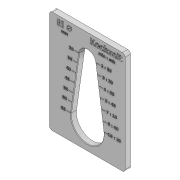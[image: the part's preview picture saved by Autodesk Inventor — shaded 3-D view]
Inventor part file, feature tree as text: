
AUTODESK INVENTOR PART (.ipt)
format: ipt  version: 2020 (Build 240168000, 168)  size: 1,938,432 bytes
history: native  units: mm
features: sketch x5, other x3, fillet x3, extrude x2
ambient origin geometry x8: Origin, YZ Plane, XZ Plane, XY Plane, X Axis, Y Axis, Z Axis, Center Point
bodies: Volumenkörper1 (feature_tree)
feature tree (13):
  extrude  "Extrusion1"  Depth=140.0mm
  extrude  "Extrusion2"  Depth=10.0mm TaperAngle=0.0deg
  other  "Prägen2"
  other  "Prägen3"
  other  "Prägen4"
  fillet  "Rundung1"  Radius=3.0mm
  fillet  "Rundung2"  Radius=3.0mm
  fillet  "Rundung3"  Radius=50.0mm
  sketch  "Skizze1"  dims[d0=190.0mm d2=140.0mm]
  sketch  "Skizze2"  dims[d3=10.0mm d4=0.0mm d11=10.0mm d12=0.0mm d23=3.0mm d24=0.0mm d29=3.0mm d30=0.0mm d31=50.0mm]
  sketch  "Skizze4"  dims[d32=45.0mm]
  sketch  "Skizze5"  dims[d33=40.0mm]
  sketch  "Skizze6"  dims[d34=35.0mm d35=30.0mm d36=55.0mm d37=60.0mm d44=2.0mm d52=3.0mm d53=0.0mm d54=1.0mm d55=5.0mm d56=70.0mm d57=2.0mm d58=2.0mm d59=2.0mm d61=2.0mm d62=2.0mm d63=2.0mm d64=2.0mm d65=2.0mm d66=2.0mm d67=2.0mm d68=2.0mm d69=2.0mm d70=2.0mm d71=43.0mm d72=20.0mm d73=20.0mm d74=5.0mm d75=5.0mm d76=5.0mm]
